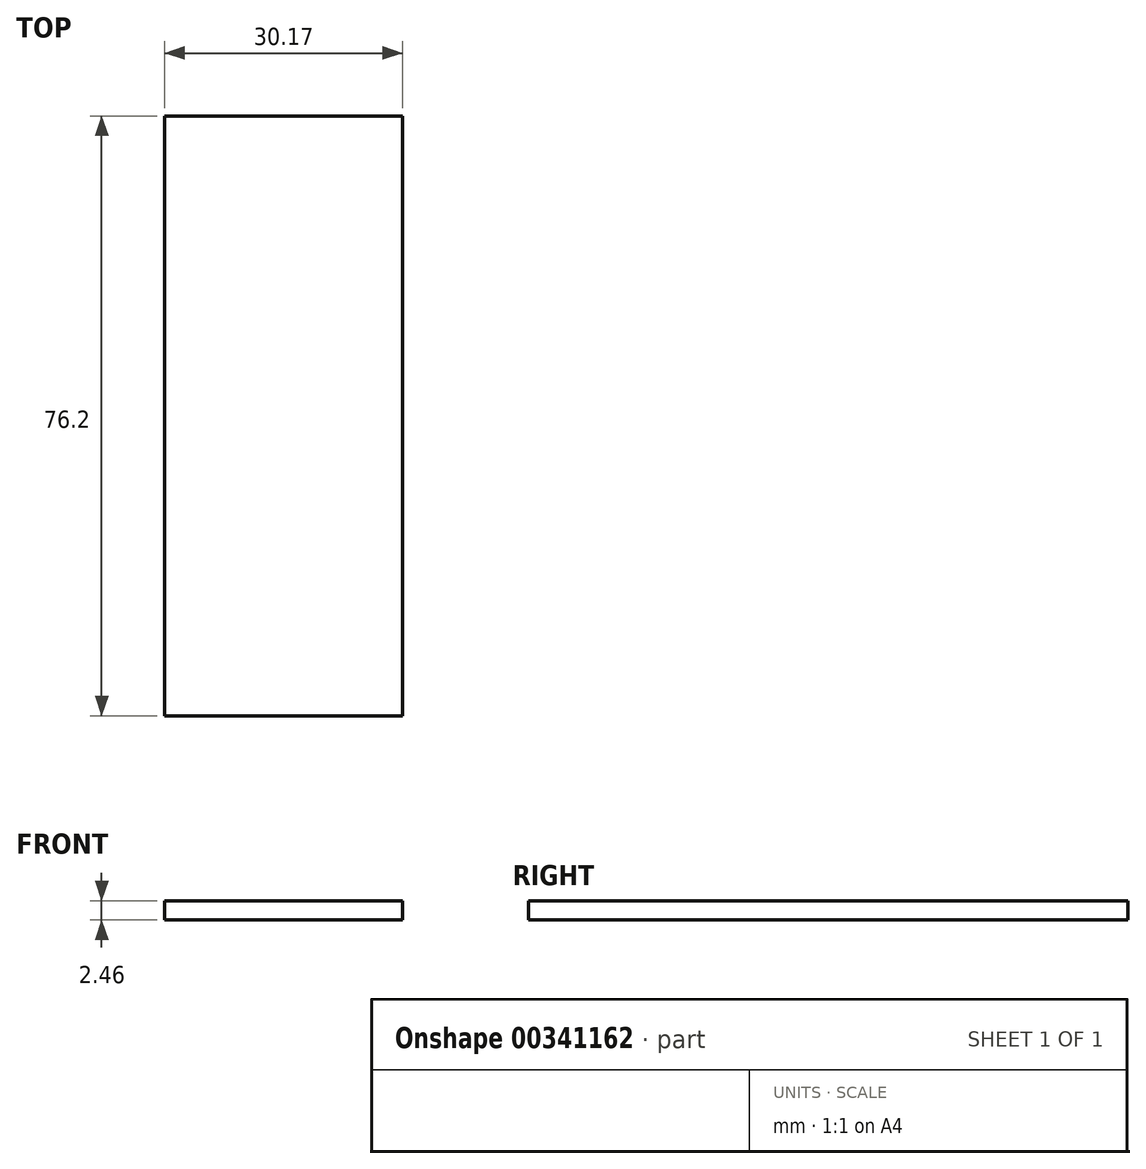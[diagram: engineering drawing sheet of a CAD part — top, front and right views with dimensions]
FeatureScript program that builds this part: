
annotation { "Feature Type Name" : "Feature", "Feature Type Description" : "" }
export const myFeature = defineFeature(function(context is Context, id is Id, definition is map)
    precondition{}
    {
        {
            var Q0;
            Q0=qCreatedBy(makeId("Top.planeOp"),FACE);
            var sketch = newSketch(context, id + "F0", { "sketchPlane" : qUnion([Q0])});
            skLineSegment(sketch, "E0.bottom", {"start": v(-11.6, 62.87) * mm, "end": v(18.58, 62.87) * mm});
            skLineSegment(sketch, "E0.top", {"start": v(-11.6, -13.33) * mm, "end": v(18.58, -13.33) * mm});
            skLineSegment(sketch, "E0.left", {"start": v(-11.6, 62.87) * mm, "end": v(-11.6, -13.33) * mm});
            skLineSegment(sketch, "E0.right", {"start": v(18.58, 62.87) * mm, "end": v(18.58, -13.33) * mm});
            skSolve(sketch);
        }
        {
            var Q0;
            Q0 = qSketchRegion(id + "F0", true);
            extrude(context, id + "F1", {"entities" : qUnion([Q0]), "depth" : 2.46 * mm});
        }
    });
